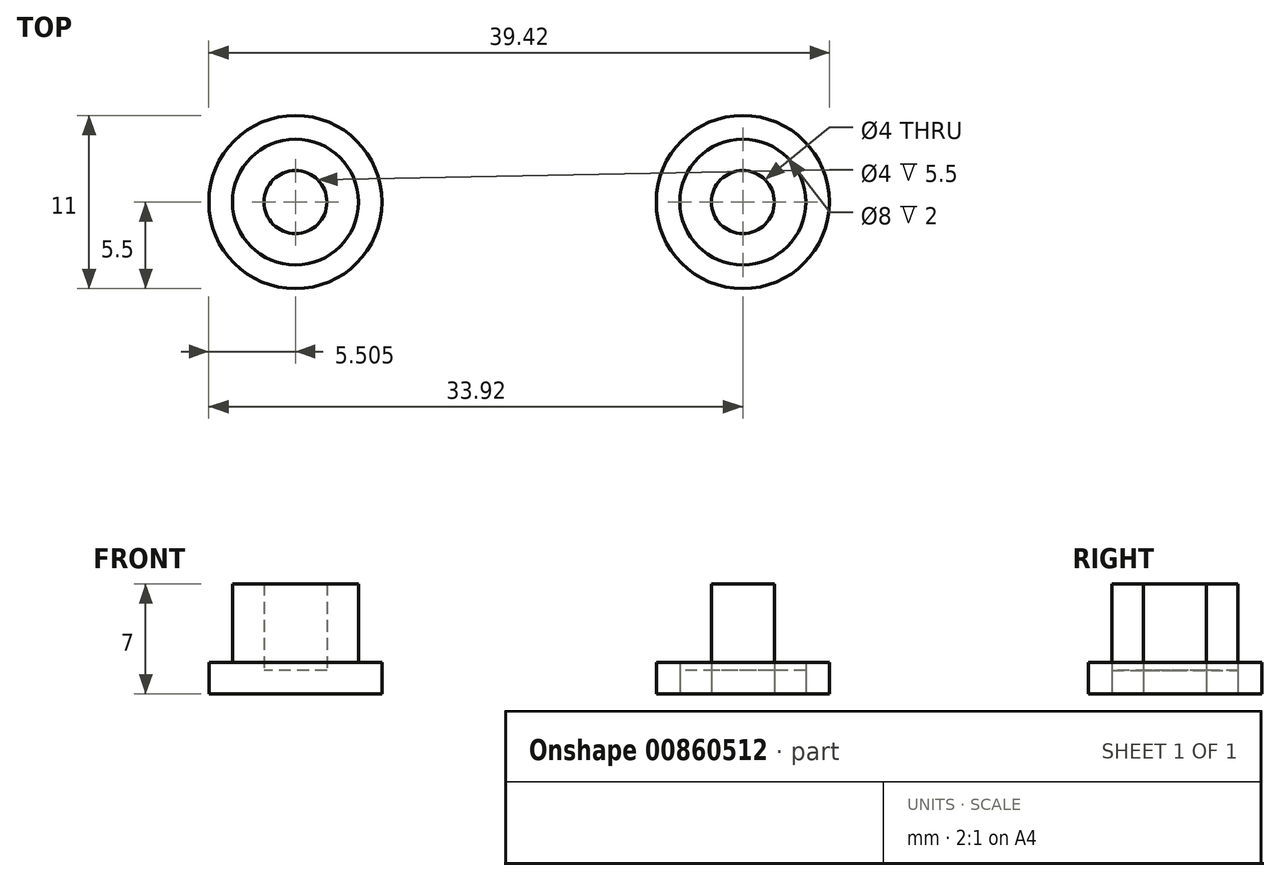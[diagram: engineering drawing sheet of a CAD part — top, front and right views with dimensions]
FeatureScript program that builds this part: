
annotation { "Feature Type Name" : "Feature", "Feature Type Description" : "" }
export const myFeature = defineFeature(function(context is Context, id is Id, definition is map)
    precondition{}
    {
        {
            var Q0;
            Q0=qCreatedBy(makeId("Top.planeOp"),FACE);
            var sketch = newSketch(context, id + "F0", { "sketchPlane" : qUnion([Q0])});
            skCircle(sketch, "E0", {"center": v(0, 0) * mm, "radius": 11 * mm});
            skCircle(sketch, "E1", {"center": v(0, 0) * mm, "radius": 5.5 * mm});
            skCircle(sketch, "E2", {"center": v(0, 0) * mm, "radius": 4 * mm});
            skCircle(sketch, "E3", {"center": v(0, 0) * mm, "radius": 2 * mm});
            skCircle(sketch, "E4", {"center": v(-28.42, 0) * mm, "radius": 11 * mm});
            skCircle(sketch, "E5", {"center": v(-28.42, 0) * mm, "radius": 5.5 * mm});
            skCircle(sketch, "E6", {"center": v(-28.42, 0) * mm, "radius": 4 * mm});
            skCircle(sketch, "E7", {"center": v(-28.42, 0) * mm, "radius": 2 * mm});
            skSolve(sketch);
        }
        {
            var Q0;
            Q0=makeQuery(id+"F0.imprint","IMPRINT",FACE,{"disambiguationData":[TD([[makeQuery(id+"F0.imprint","IMPRINT",EDGE,{"derivedFrom":sQuery(id+"F0.wireOp",EDGE,"E1")}),1.0]])]});
            var Q1;
            Q1=makeQuery(id+"F0.imprint","IMPRINT",FACE,{"disambiguationData":[TD([[makeQuery(id+"F0.imprint","IMPRINT",EDGE,{"derivedFrom":sQuery(id+"F0.wireOp",EDGE,"E5")}),1.0]])]});
            extrude(context, id + "F1", {"entities" : qUnion([Q0, Q1]), "depth" : 2 * mm, "offsetDistance" : 25 * mm});
        }
        {
            var Q0;
            Q0=makeQuery(id+"F0.imprint","IMPRINT",FACE,{"disambiguationData":[TD([[makeQuery(id+"F0.imprint","IMPRINT",EDGE,{"derivedFrom":sQuery(id+"F0.wireOp",EDGE,"E6")}),1.0]])]});
            var Q1;
            Q1=makeQuery(id+"F0.imprint","IMPRINT",FACE,{"disambiguationData":[TD([[makeQuery(id+"F0.imprint","IMPRINT",EDGE,{"derivedFrom":sQuery(id+"F0.wireOp",EDGE,"E3")}),1.0]])]});
            extrude(context, id + "F2", {"entities" : qUnion([Q0, Q1]), "operationType" : NewBodyOperationType.ADD, "depth" : 7 * mm, "offsetDistance" : 25 * mm});
        }
        {
            var Q0;
            Q0=makeQuery(id+"F0.imprint","IMPRINT",FACE,{"disambiguationData":[TD([[makeQuery(id+"F0.imprint","IMPRINT",EDGE,{"derivedFrom":sQuery(id+"F0.wireOp",EDGE,"E2")}),1.0]])]});
            extrude(context, id + "F3", {"entities" : qUnion([Q0]), "depth" : 1.5 * mm, "offsetDistance" : 25 * mm});
        }
        {
            var Q0;
            Q0=makeQuery(id+"F0.imprint","IMPRINT",FACE,{"disambiguationData":[TD([[makeQuery(id+"F0.imprint","IMPRINT",EDGE,{"derivedFrom":sQuery(id+"F0.wireOp",EDGE,"E7")}),1.0]])]});
            extrude(context, id + "F4", {"entities" : qUnion([Q0]), "operationType" : NewBodyOperationType.ADD, "depth" : 1.5 * mm, "offsetDistance" : 25 * mm});
        }
    });
